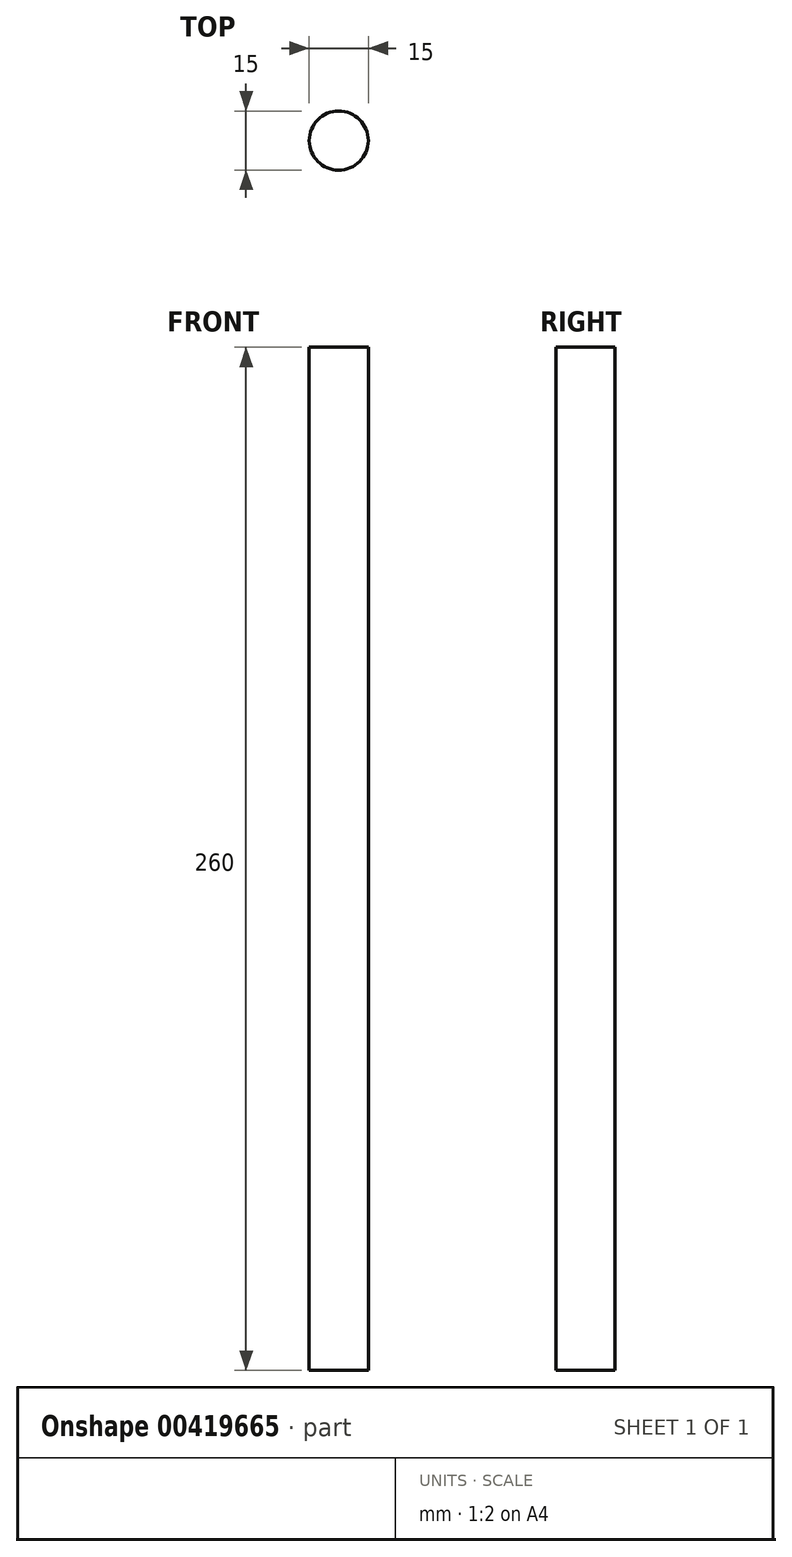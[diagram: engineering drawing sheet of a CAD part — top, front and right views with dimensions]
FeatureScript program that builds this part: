
annotation { "Feature Type Name" : "Feature", "Feature Type Description" : "" }
export const myFeature = defineFeature(function(context is Context, id is Id, definition is map)
    precondition{}
    {
        {
            var Q0;
            Q0=qCreatedBy(makeId("Top.planeOp"),FACE);
            var sketch = newSketch(context, id + "F0", { "sketchPlane" : qUnion([Q0])});
            skCircle(sketch, "E0", {"center": v(0, 0) * mm, "radius": 7.5 * mm});
            skSolve(sketch);
        }
        {
            var Q0;
            Q0=makeQuery(id+"F0.imprint","IMPRINT",FACE,{"disambiguationData":[TD([[makeQuery(id+"F0.imprint","IMPRINT",EDGE,{"derivedFrom":sQuery(id+"F0.wireOp",EDGE,"E0")}),1.0]])]});
            extrude(context, id + "F1", {"entities" : qUnion([Q0]), "depth" : 260 * mm});
        }
    });
